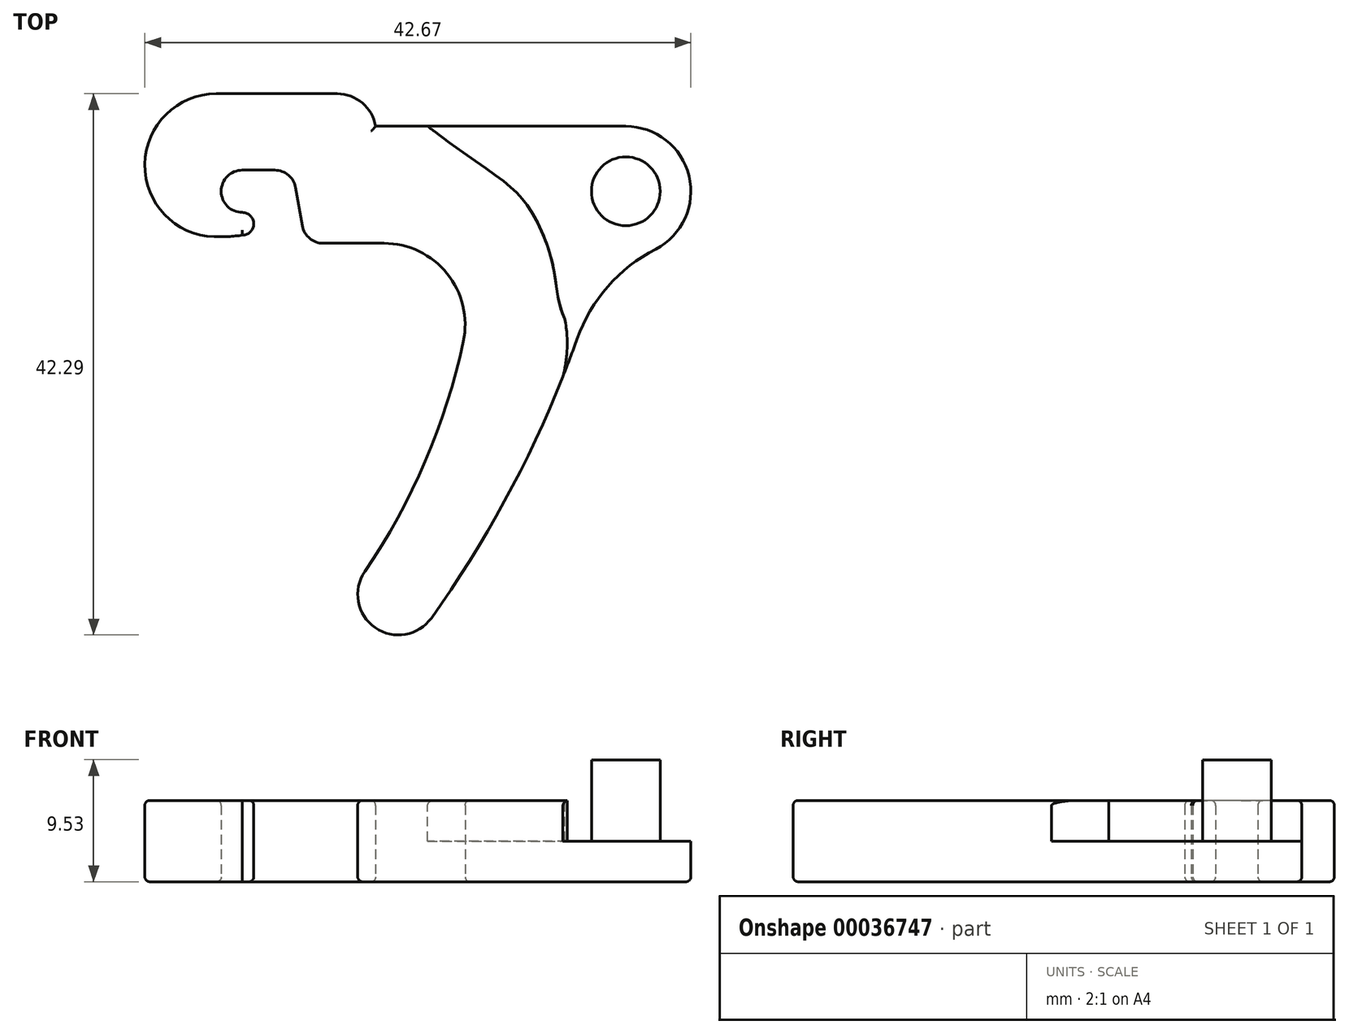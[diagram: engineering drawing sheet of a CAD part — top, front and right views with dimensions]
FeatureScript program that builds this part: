
annotation { "Feature Type Name" : "Feature", "Feature Type Description" : "" }
export const myFeature = defineFeature(function(context is Context, id is Id, definition is map)
    precondition{}
    {
        {
            var Q0;
            Q0=qCreatedBy(makeId("Top.planeOp"),FACE);
            var sketch = newSketch(context, id + "F0", { "sketchPlane" : qUnion([Q0])});
            skArc(sketch, "E0", {"start": v(2.33, -4.51) * mm, "mid": v(4.94, 1.2) * mm, "end": v(0, 5.08) * mm});
            skArc(sketch, "E1", {"start": v(-29.97, 1.65) * mm, "mid": v(-31.62, 0) * mm, "end": v(-29.97, -1.65) * mm});
            skArc(sketch, "E2", {"start": v(-25.8, 0.29) * mm, "mid": v(-26.37, 1.26) * mm, "end": v(-27.43, 1.65) * mm});
            skLineSegment(sketch, "E3", {"start": v(-29.97, 1.65) * mm, "end": v(-27.43, 1.65) * mm});
            skLineSegment(sketch, "E4", {"start": v(-25.8, 0.29) * mm, "end": v(-25.28, -2.7) * mm});
            skArc(sketch, "E5", {"start": v(-25.28, -2.7) * mm, "mid": v(-24.71, -3.68) * mm, "end": v(-23.65, -4.06) * mm});
            skLineSegment(sketch, "E6", {"start": v(-23.65, -4.06) * mm, "end": v(-18.9, -4.06) * mm});
            skArc(sketch, "E7", {"start": v(-12.7, -11.75) * mm, "mid": v(-13.97, -6.42) * mm, "end": v(-18.9, -4.06) * mm});
            skArc(sketch, "E8", {"start": v(-20.4, -29.7) * mm, "mid": v(-15.68, -21.1) * mm, "end": v(-12.7, -11.75) * mm});
            skArc(sketch, "E9", {"start": v(-20.4, -29.7) * mm, "mid": v(-19.6, -34.1) * mm, "end": v(-15.2, -33.34) * mm});
            skArc(sketch, "E10", {"start": v(-15.2, -33.34) * mm, "mid": v(-8.75, -22.83) * mm, "end": v(-3.8, -11.54) * mm});
            skLineSegment(sketch, "E11", {"start": v(0, 5.08) * mm, "end": v(-19.56, 5.08) * mm});
            skArc(sketch, "E12", {"start": v(-19.56, 5.08) * mm, "mid": v(-20.6, 6.9) * mm, "end": v(-22.56, 7.62) * mm});
            skLineSegment(sketch, "E13", {"start": v(-22.56, 7.62) * mm, "end": v(-32, 7.62) * mm});
            skArc(sketch, "E14", {"start": v(-29.97, -3.43) * mm, "mid": v(-29.08, -2.54) * mm, "end": v(-29.97, -1.65) * mm});
            skArc(sketch, "E15", {"start": v(2.33, -4.51) * mm, "mid": v(-1.4, -7.44) * mm, "end": v(-3.8, -11.54) * mm});
            skArc(sketch, "E16", {"start": v(-32, 7.62) * mm, "mid": v(-37.6, 2.12) * mm, "end": v(-32.17, -3.55) * mm});
            skArc(sketch, "E17", {"start": v(-32.17, -3.55) * mm, "mid": v(-31.07, -3.54) * mm, "end": v(-29.97, -3.43) * mm});
            skSolve(sketch);
        }
        {
            var Q0;
            Q0 = qSketchRegion(id + "F0", true);
            extrude(context, id + "F1", {"entities" : qUnion([Q0]), "depth" : 6.35 * mm});
        }
        {
            var Q0;
            Q0=makeQuery(id+"F1.opExtrude","CAP_FACE",FACE,{"disambiguationData":[OSD([sQuery(id+"F0.wireOp",EDGE,"E0"),sQuery(id+"F0.wireOp",EDGE,"E1"),sQuery(id+"F0.wireOp",EDGE,"E2"),sQuery(id+"F0.wireOp",EDGE,"E3"),sQuery(id+"F0.wireOp",EDGE,"E4"),sQuery(id+"F0.wireOp",EDGE,"E5"),sQuery(id+"F0.wireOp",EDGE,"E6"),sQuery(id+"F0.wireOp",EDGE,"E7"),sQuery(id+"F0.wireOp",EDGE,"E8"),sQuery(id+"F0.wireOp",EDGE,"E9"),sQuery(id+"F0.wireOp",EDGE,"E10"),sQuery(id+"F0.wireOp",EDGE,"E11"),sQuery(id+"F0.wireOp",EDGE,"E12"),sQuery(id+"F0.wireOp",EDGE,"E13"),sQuery(id+"F0.wireOp",EDGE,"E14"),sQuery(id+"F0.wireOp",EDGE,"E15"),sQuery(id+"F0.wireOp",EDGE,"E16"),sQuery(id+"F0.wireOp",EDGE,"E17")])],"isStart":false});
            var sketch = newSketch(context, id + "F2", { "sketchPlane" : qUnion([Q0])});
            skArc(sketch, "E18", {"start": v(2.33, -4.51) * mm, "mid": v(4.94, 1.2) * mm, "end": v(0, 5.08) * mm});
            skLineSegment(sketch, "E19", {"start": v(0, 5.08) * mm, "end": v(-15.5, 5.08) * mm});
            skArc(sketch, "E20", {"start": v(2.33, -4.51) * mm, "mid": v(-1.4, -7.45) * mm, "end": v(-3.8, -11.54) * mm});
            skFitSpline(sketch, "E21", {"points": [v(-15.5, 5.08) * mm, v(-8.64, 0) * mm, v(-6.86, -2.54) * mm, v(-5.59, -6.35) * mm, v(-3.8, -11.54) * mm], "startDerivative": vector(33.89, -25.9) * mm, "endDerivative": vector(18.15, -23.16) * mm});
            skSolve(sketch);
        }
        {
            var Q0;
            Q0=makeQuery(id+"F2.imprint","IMPRINT",FACE,{"disambiguationData":[TD([[makeQuery(id+"F2.imprint","IMPRINT",EDGE,{"derivedFrom":sQuery(id+"F2.wireOp",EDGE,"E20")}),-1.0]])]});
            var Q1;
            Q1=makeQuery(id+"F2.imprint","IMPRINT",FACE,{"disambiguationData":[TD([[makeQuery(id+"F2.imprint","IMPRINT",EDGE,{"derivedFrom":sQuery(id+"F2.wireOp",EDGE,"E18")}),1.0]])]});
            var Q2;
            Q2=makeQuery(id+"F1.opExtrude","CAP_FACE",FACE,{"disambiguationData":[OSD([sQuery(id+"F0.wireOp",EDGE,"E0"),sQuery(id+"F0.wireOp",EDGE,"E1"),sQuery(id+"F0.wireOp",EDGE,"E2"),sQuery(id+"F0.wireOp",EDGE,"E3"),sQuery(id+"F0.wireOp",EDGE,"E4"),sQuery(id+"F0.wireOp",EDGE,"E5"),sQuery(id+"F0.wireOp",EDGE,"E6"),sQuery(id+"F0.wireOp",EDGE,"E7"),sQuery(id+"F0.wireOp",EDGE,"E8"),sQuery(id+"F0.wireOp",EDGE,"E9"),sQuery(id+"F0.wireOp",EDGE,"E10"),sQuery(id+"F0.wireOp",EDGE,"E11"),sQuery(id+"F0.wireOp",EDGE,"E12"),sQuery(id+"F0.wireOp",EDGE,"E13"),sQuery(id+"F0.wireOp",EDGE,"E14"),sQuery(id+"F0.wireOp",EDGE,"E15"),sQuery(id+"F0.wireOp",EDGE,"E16"),sQuery(id+"F0.wireOp",EDGE,"E17")])],"isStart":true});
            extrude(context, id + "F3", {"entities" : qUnion([Q0, Q1, Q2]), "operationType" : NewBodyOperationType.REMOVE, "oppositeDirection" : true, "depth" : 3.17 * mm});
        }
        {
            var Q0;
            Q0=makeQuery(id+"F3.boolean.opBoolean","COPY",FACE,{"derivedFrom":makeQuery(id+"F3.opExtrude","CAP_FACE",FACE,{"disambiguationData":[OSD([sQuery(id+"F2.wireOp",EDGE,"E18"),sQuery(id+"F2.wireOp",EDGE,"E19"),sQuery(id+"F2.wireOp",EDGE,"E20"),sQuery(id+"F2.wireOp",EDGE,"E21")])],"isStart":false})});
            var sketch = newSketch(context, id + "F4", { "sketchPlane" : qUnion([Q0])});
            skCircle(sketch, "E22", {"center": v(0, 0) * mm, "radius": 2.69 * mm});
            skSolve(sketch);
        }
        {
            var Q0;
            Q0 = qSketchRegion(id + "F4", true);
            extrude(context, id + "F5", {"entities" : qUnion([Q0]), "operationType" : NewBodyOperationType.ADD, "depth" : 6.35 * mm});
        }
        {
            var Q0;
            Q0=makeQuery(id+"F1.opExtrude","CAP_FACE",FACE,{"disambiguationData":[OSD([sQuery(id+"F0.wireOp",EDGE,"E0"),sQuery(id+"F0.wireOp",EDGE,"E1"),sQuery(id+"F0.wireOp",EDGE,"E2"),sQuery(id+"F0.wireOp",EDGE,"E3"),sQuery(id+"F0.wireOp",EDGE,"E4"),sQuery(id+"F0.wireOp",EDGE,"E5"),sQuery(id+"F0.wireOp",EDGE,"E6"),sQuery(id+"F0.wireOp",EDGE,"E7"),sQuery(id+"F0.wireOp",EDGE,"E8"),sQuery(id+"F0.wireOp",EDGE,"E9"),sQuery(id+"F0.wireOp",EDGE,"E10"),sQuery(id+"F0.wireOp",EDGE,"E11"),sQuery(id+"F0.wireOp",EDGE,"E12"),sQuery(id+"F0.wireOp",EDGE,"E13"),sQuery(id+"F0.wireOp",EDGE,"E14"),sQuery(id+"F0.wireOp",EDGE,"E15"),sQuery(id+"F0.wireOp",EDGE,"E16"),sQuery(id+"F0.wireOp",EDGE,"E17")])],"isStart":false});
            var sketch = newSketch(context, id + "F6", { "sketchPlane" : qUnion([Q0])});
            skArc(sketch, "E23", {"start": v(-4.92, -14.5) * mm, "mid": v(-4.6, -12.25) * mm, "end": v(-4.76, -10) * mm});
            skLineSegment(sketch, "E24", {"start": v(-4.92, -14.5) * mm, "end": v(4.61, -8.09) * mm});
            skLineSegment(sketch, "E25", {"start": v(4.61, -8.09) * mm, "end": v(-4.76, -10) * mm});
            skSolve(sketch);
        }
        {
            var Q0;
            Q0 = qSketchRegion(id + "F6", true);
            extrude(context, id + "F7", {"entities" : qUnion([Q0]), "operationType" : NewBodyOperationType.REMOVE, "oppositeDirection" : true, "depth" : 3.17 * mm});
        }
        {
            var Q0;
            Q0=makeQuery(id+"F1.opExtrude","CAP_EDGE",EDGE,{"disambiguationData":[OSD([sQuery(id+"F0.wireOp",EDGE,"E10")])],"isStart":false});
            var Q1;
            Q1=makeQuery(id+"F1.opExtrude","CAP_EDGE",EDGE,{"disambiguationData":[OSD([sQuery(id+"F0.wireOp",EDGE,"E9")])],"isStart":false});
            var Q2;
            Q2=makeQuery(id+"F1.opExtrude","CAP_EDGE",EDGE,{"disambiguationData":[OSD([sQuery(id+"F0.wireOp",EDGE,"E8")])],"isStart":false});
            var Q3;
            Q3=makeQuery(id+"F1.opExtrude","CAP_EDGE",EDGE,{"disambiguationData":[OSD([sQuery(id+"F0.wireOp",EDGE,"E7")])],"isStart":false});
            var Q4;
            Q4=makeQuery(id+"F1.opExtrude","CAP_EDGE",EDGE,{"disambiguationData":[OSD([sQuery(id+"F0.wireOp",EDGE,"E6")])],"isStart":false});
            var Q5;
            Q5=makeQuery(id+"F1.opExtrude","CAP_EDGE",EDGE,{"disambiguationData":[OSD([sQuery(id+"F0.wireOp",EDGE,"E5")])],"isStart":false});
            var Q6;
            Q6=makeQuery(id+"F1.opExtrude","CAP_EDGE",EDGE,{"disambiguationData":[OSD([sQuery(id+"F0.wireOp",EDGE,"E4")])],"isStart":false});
            var Q7;
            Q7=makeQuery(id+"F1.opExtrude","CAP_EDGE",EDGE,{"disambiguationData":[OSD([sQuery(id+"F0.wireOp",EDGE,"E2")])],"isStart":false});
            var Q8;
            Q8=makeQuery(id+"F1.opExtrude","CAP_EDGE",EDGE,{"disambiguationData":[OSD([sQuery(id+"F0.wireOp",EDGE,"E3")])],"isStart":false});
            var Q9;
            Q9=makeQuery(id+"F1.opExtrude","CAP_EDGE",EDGE,{"disambiguationData":[OSD([sQuery(id+"F0.wireOp",EDGE,"E1")])],"isStart":false});
            var Q10;
            Q10=makeQuery(id+"F1.opExtrude","CAP_EDGE",EDGE,{"disambiguationData":[OSD([sQuery(id+"F0.wireOp",EDGE,"E14")])],"isStart":false});
            var Q11;
            Q11=makeQuery(id+"F1.opExtrude","CAP_EDGE",EDGE,{"disambiguationData":[OSD([sQuery(id+"F0.wireOp",EDGE,"E17")])],"isStart":false});
            var Q12;
            Q12=makeQuery(id+"F1.opExtrude","CAP_EDGE",EDGE,{"disambiguationData":[OSD([sQuery(id+"F0.wireOp",EDGE,"E16")])],"isStart":false});
            var Q13;
            Q13=makeQuery(id+"F1.opExtrude","CAP_EDGE",EDGE,{"disambiguationData":[OSD([sQuery(id+"F0.wireOp",EDGE,"E13")])],"isStart":false});
            var Q14;
            Q14=makeQuery(id+"F1.opExtrude","CAP_EDGE",EDGE,{"disambiguationData":[OSD([sQuery(id+"F0.wireOp",EDGE,"E12")])],"isStart":false});
            var Q15;
            Q15=makeQuery(id+"F1.opExtrude","CAP_EDGE",EDGE,{"disambiguationData":[OSD([sQuery(id+"F0.wireOp",EDGE,"E11")])],"isStart":false});
            var Q16;
            Q16=makeQuery(id+"F3.boolean.opBoolean","COPY",EDGE,{"derivedFrom":makeQuery(id+"F3.opExtrude","CAP_EDGE",EDGE,{"disambiguationData":[OSD([sQuery(id+"F2.wireOp",EDGE,"E21")])],"isStart":true})});
            var Q17;
            Q17=makeQuery(id+"F7.boolean.opBoolean","COPY",EDGE,{"derivedFrom":makeQuery(id+"F7.opExtrude","CAP_EDGE",EDGE,{"disambiguationData":[OSD([sQuery(id+"F6.wireOp",EDGE,"E23")])],"isStart":true})});
            fillet(context, id + "F8", {"entities" : qUnion([Q0, Q1, Q2, Q3, Q4, Q5, Q6, Q7, Q8, Q9, Q10, Q11, Q12, Q13, Q14, Q15, Q16, Q17]), "radius" : 0.38 * mm, "tangentPropagation" : true, "allowEdgeOverflow" : false});
        }
        {
            var Q0;
            Q0=makeQuery(id+"F1.opExtrude","CAP_FACE",FACE,{"disambiguationData":[OSD([sQuery(id+"F0.wireOp",EDGE,"E0"),sQuery(id+"F0.wireOp",EDGE,"E1"),sQuery(id+"F0.wireOp",EDGE,"E2"),sQuery(id+"F0.wireOp",EDGE,"E3"),sQuery(id+"F0.wireOp",EDGE,"E4"),sQuery(id+"F0.wireOp",EDGE,"E5"),sQuery(id+"F0.wireOp",EDGE,"E6"),sQuery(id+"F0.wireOp",EDGE,"E7"),sQuery(id+"F0.wireOp",EDGE,"E8"),sQuery(id+"F0.wireOp",EDGE,"E9"),sQuery(id+"F0.wireOp",EDGE,"E10"),sQuery(id+"F0.wireOp",EDGE,"E11"),sQuery(id+"F0.wireOp",EDGE,"E12"),sQuery(id+"F0.wireOp",EDGE,"E13"),sQuery(id+"F0.wireOp",EDGE,"E14"),sQuery(id+"F0.wireOp",EDGE,"E15"),sQuery(id+"F0.wireOp",EDGE,"E16"),sQuery(id+"F0.wireOp",EDGE,"E17")])],"isStart":true});
            fillet(context, id + "F9", {"entities" : qUnion([Q0]), "radius" : 0.38 * mm, "tangentPropagation" : true, "allowEdgeOverflow" : false});
        }
    });
